# Revit family: Клапан для отключения радиатора с высокой пропускной способностью HERZ-RL-1-E, угловой 3724
name_source: partatom
category: Rohrzubehör
units: mm (PartAtom-declared; Revit-internal decimal feet)

## family parameters
Arbeitsebenenbasiert = Nein
Beim Laden mit Abzugskörper schneiden = Nein
Bemaßung runder Anschluss = Durchmesser verwenden
Gemeinsam genutzt = Nein
Immer vertikal = Nein
OmniClass-Nummer = 23.65.55.14
OmniClass-Titel = Valves for Liquid Services
Teiletyp = Unterbricht

## types (1)
- Клапан для отключения радиатора с высокой пропускной способностью HERZ-RL-1-E, угловой 3724
    H04 = 17 mm
    H05 = 8 mm  [stored 0.0262467 ft]
    H06 = 14 mm  [stored 0.0459318 ft]
    Hersteller = HERZ Armaturen Ges.m.b.H.
    L05 = 19.5 mm  [stored 0.0639764 ft]
    R01 = 18 mm  [stored 0.0590551 ft]
    R02 = 17.5 mm
    R03 = 11.75 mm
    R04 = 10 mm  [stored 0.0328084 ft]
    S01 = 10 mm  [stored 0.0328084 ft]
    S04 = 45 mm
    SCRNCODE = 05;01;02
    SCRNSEQ = ARM;ARM_TYP="ALLF";2
    URL = www.herz-armaturen.ru
    W01 = 120.00°
    Исполнение = Стандартные модели с резьбовой муфтой в никелированном исполнении.
    Корпус = Никелированная латунь
    Макс. рабочая температура = 120 °C
    Макс. рабочее давление = 1000000.0 Pa
    Область применения = Система водяного отопления. С помощью установки радиаторных запорных клапанов возможно осуществить перекрытие обратного потока нагревательных приборов. При одновременном перекрытии с клапаном на подающем трубопроводе возможен демонтаж радиатора в системе, которая находится под давлением.
    Среда = Качество воды в соответствии с ÖNORM H 5195 или директивой VDI 2035.

note: [stored X ft] marks values corroborated as IEEE doubles in the binary element streams (Revit-internal decimal feet)
